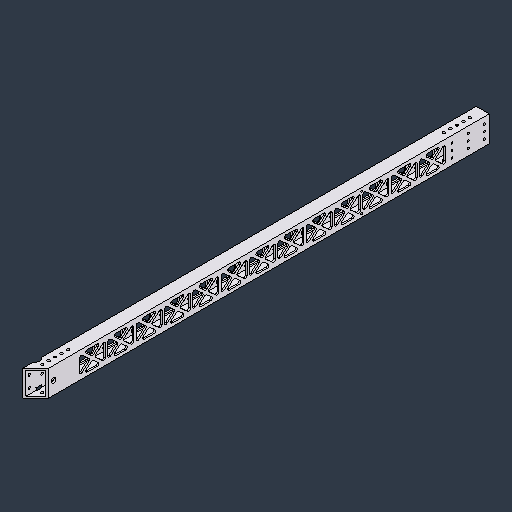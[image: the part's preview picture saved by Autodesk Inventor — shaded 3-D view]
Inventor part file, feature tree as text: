
AUTODESK INVENTOR PART (.ipt)
format: ipt  version: 2024.3 (Build 283343000, 343)  size: 725,504 bytes
history: native  units: in
note: dims shown in document units (in); Inventor stores cm internally (conversion verified against a paired STEP export)
features: sketch x9, hole x5, extrude x4, pattern_linear x2, mirror x2, fillet x1, projected_geometry x1
ambient origin geometry x8: Origin, YZ Plane, XZ Plane, XY Plane, X Axis, Y Axis, Z Axis, Center Point
bodies: Solid1 (feature_tree)
feature tree (24):
  extrude  "Extrusion1"  Depth=2.0in
  extrude  "Extrusion2"  Depth=0.125in TaperAngle=0.0deg
  hole  "Hole1"  [1 undecoded]
  hole  "Hole2"  [1 undecoded]
  hole  "Hole3"  [1 undecoded]
  hole  "Hole4"  [1 undecoded]
  hole  "Hole5"  [1 undecoded]
  pattern_linear  "Rectangular Pattern2"  Spacing1=0.3in  [1 undecoded]
  extrude  "Extrusion3"  TaperAngle=45.0deg  [1 undecoded]
  extrude  "Extrusion4"  Depth=1.5in
  fillet  "Fillet1"  Radius=0.1875in
  pattern_linear  "Rectangular Pattern1"  Spacing1=2.0in  [1 undecoded]
  mirror  "Mirror2"
  mirror  "Mirror3"
  sketch  "Sketch1"  dims[d0=1.0in d1=2.0in]
  sketch  "Sketch2"  dims[d2=0.125in d3=35.0in d4=0.0in]
  projected_geometry  "Projected Loop1"
  sketch  "Sketch4"  dims[d7=0.0in d8=0.0in d9=0.5in]
  sketch  "Sketch5"  dims[d11=1.9685in d13=0.5in d14=0.3937in d16=1.0in]
  sketch  "Sketch6"  dims[d18=0.201in d19=0.38in d20=0.375in d21=0.25in d22=0.5635in d23=1.0in d24=0.8108in d25=16.125in]
  sketch  "Sketch7"  dims[d26=0.196in d27=0.75in d28=0.375in d29=0.5in d30=0.5635in d31=1.0in d32=0.8108in d33=1.0in]
  sketch  "Sketch8"  dims[d34=0.875in]
  sketch  "Sketch9"  dims[d35=0.196in d36=0.75in d37=0.375in d38=0.19in d39=0.5635in d40=1.0in d41=0.8108in d42=0.1875in]
  sketch  "Sketch10"  dims[d43=1.125in d44=0.75in d45=0.3in d46=0.0in d47=45.0deg d50=1.5in d51=0.1875in d52=2.0in d53=0.0in d54=0.0in d55=0.125in d56=5.1181in d58=2.1875in d59=16.5in d60=1.0in d61=1.0in d62=0.375in d63=0.156in d64=0.38in d65=0.385in d66=0.077in d67=0.5635in d68=0.536in d69=0.8108in d70=1.1811in d72=1.25in d81=0.156in d82=0.38in d83=0.385in d84=0.077in d85=0.5635in d86=0.536in d87=0.8108in d88=1.5in d89=9.8438in]
note: 8 required parameter values undecoded (feature->parameter linkage not recoverable at this tier; creation-order binding heuristic only, values carry confidence <= 0.55)
